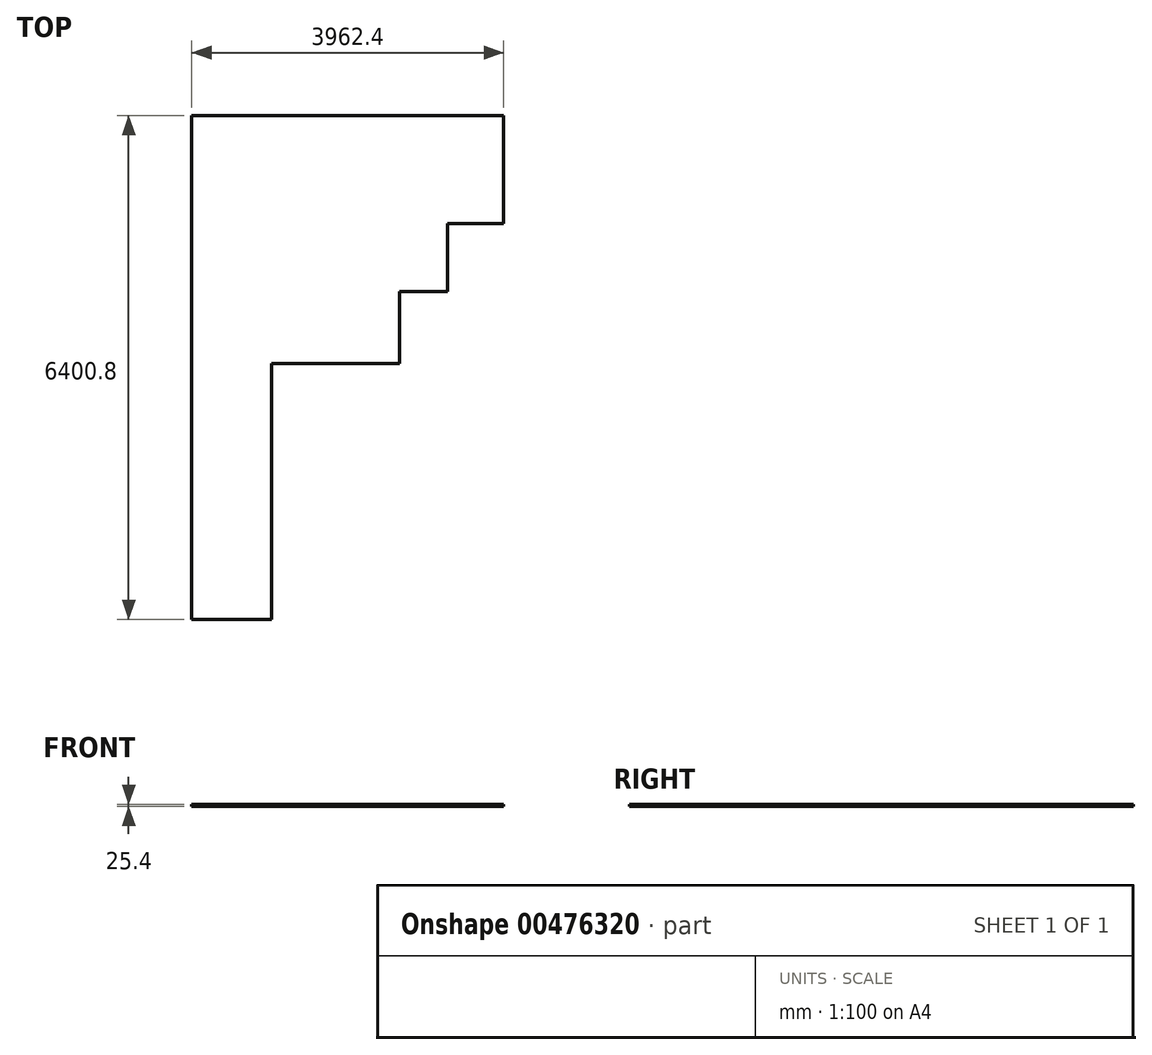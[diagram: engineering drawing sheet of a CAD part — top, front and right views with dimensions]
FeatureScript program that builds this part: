
annotation { "Feature Type Name" : "Feature", "Feature Type Description" : "" }
export const myFeature = defineFeature(function(context is Context, id is Id, definition is map)
    precondition{}
    {
        {
            var Q0;
            Q0=qCreatedBy(makeId("Top.planeOp"),FACE);
            var sketch = newSketch(context, id + "F0", { "sketchPlane" : qUnion([Q0])});
            skLineSegment(sketch, "E0", {"start": v(0, 0) * mm, "end": v(0, 6400.8) * mm});
            skLineSegment(sketch, "E1", {"start": v(0, 6400.8) * mm, "end": v(3962.4, 6400.8) * mm});
            skLineSegment(sketch, "E2", {"start": v(3962.4, 6400.8) * mm, "end": v(3962.4, 5029.2) * mm});
            skLineSegment(sketch, "E3", {"start": v(3962.4, 5029.2) * mm, "end": v(3251.2, 5029.2) * mm});
            skLineSegment(sketch, "E4", {"start": v(3251.2, 5029.2) * mm, "end": v(3251.2, 4165.6) * mm});
            skLineSegment(sketch, "E5", {"start": v(3251.2, 4165.6) * mm, "end": v(2641.6, 4165.6) * mm});
            skLineSegment(sketch, "E6", {"start": v(2641.6, 4165.6) * mm, "end": v(2641.6, 3251.2) * mm});
            skLineSegment(sketch, "E7", {"start": v(2641.6, 3251.2) * mm, "end": v(1016, 3251.2) * mm});
            skLineSegment(sketch, "E8", {"start": v(1016, 3251.2) * mm, "end": v(1016, 0) * mm});
            skLineSegment(sketch, "E9", {"start": v(1016, 0) * mm, "end": v(0, 0) * mm});
            skSolve(sketch);
        }
        {
            var Q0;
            Q0 = qSketchRegion(id + "F0", true);
            extrude(context, id + "F1", {"entities" : qUnion([Q0]), "oppositeDirection" : true, "depth" : 25.4 * mm});
        }
    });
